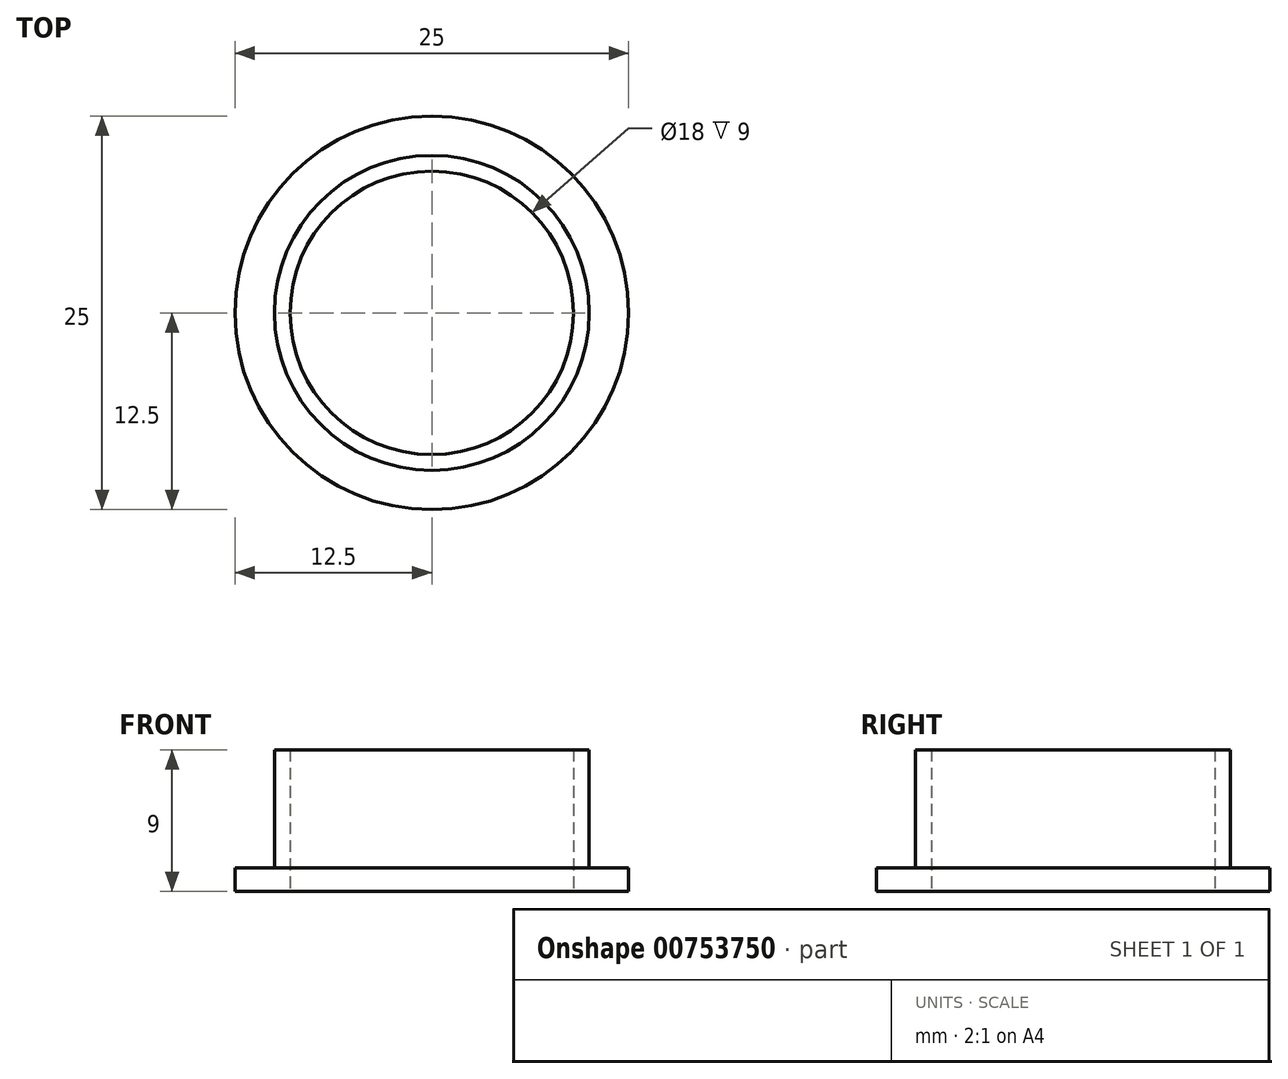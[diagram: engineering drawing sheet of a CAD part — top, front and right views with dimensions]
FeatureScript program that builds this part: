
annotation { "Feature Type Name" : "Feature", "Feature Type Description" : "" }
export const myFeature = defineFeature(function(context is Context, id is Id, definition is map)
    precondition{}
    {
        {
            var Q0;
            Q0=qCreatedBy(makeId("Top.planeOp"),FACE);
            var sketch = newSketch(context, id + "F0", { "sketchPlane" : qUnion([Q0])});
            skCircle(sketch, "E0", {"center": v(0, 0) * mm, "radius": 9 * mm});
            skSolve(sketch);
        }
        {
            var Q0;
            Q0=qCreatedBy(makeId("Front.planeOp"),FACE);
            var sketch = newSketch(context, id + "F1", { "sketchPlane" : qUnion([Q0])});
            skLineSegment(sketch, "E1", {"start": v(9, 0) * mm, "end": v(12, 0) * mm});
            skLineSegment(sketch, "E2", {"start": v(9, 9) * mm, "end": v(10, 9) * mm});
            skLineSegment(sketch, "E3", {"start": v(10, 9) * mm, "end": v(10, 1.5) * mm});
            skLineSegment(sketch, "E4", {"start": v(10, 1.5) * mm, "end": v(12, 1.5) * mm});
            skLineSegment(sketch, "E5", {"start": v(9, 9) * mm, "end": v(9, 0) * mm});
            skLineSegment(sketch, "E6", {"start": v(12, 0) * mm, "end": v(12.5, 0) * mm});
            skLineSegment(sketch, "E7", {"start": v(12.5, 0) * mm, "end": v(12.5, 1.5) * mm});
            skLineSegment(sketch, "E8", {"start": v(12.5, 1.5) * mm, "end": v(12, 1.5) * mm});
            skSolve(sketch);
        }
        {
            var Q0;
            Q0=qCreatedBy(makeId("Front.planeOp"),FACE);
            var sketch = newSketch(context, id + "F2", { "sketchPlane" : qUnion([Q0])});
            skLineSegment(sketch, "E9", {"start": v(0, 0) * mm, "end": v(0, 9.7) * mm});
            skSolve(sketch);
        }
        {
            var Q0;
            Q0=makeQuery(id+"F1.imprint","IMPRINT",FACE,{"disambiguationData":[TD([[makeQuery(id+"F1.imprint","IMPRINT",EDGE,{"derivedFrom":sQuery(id+"F1.wireOp",EDGE,"E1")}),1.0]])]});
            var Q1;
            Q1=sQuery(id+"F2.wireOp",EDGE,"E9");
            revolve(context, id + "F3", {"surfaceOperationType" : NewSurfaceOperationType.NEW, "entities" : qUnion([Q0]), "axis" : qUnion([Q1]), "revolveType" : RevolveType.FULL});
        }
    });
